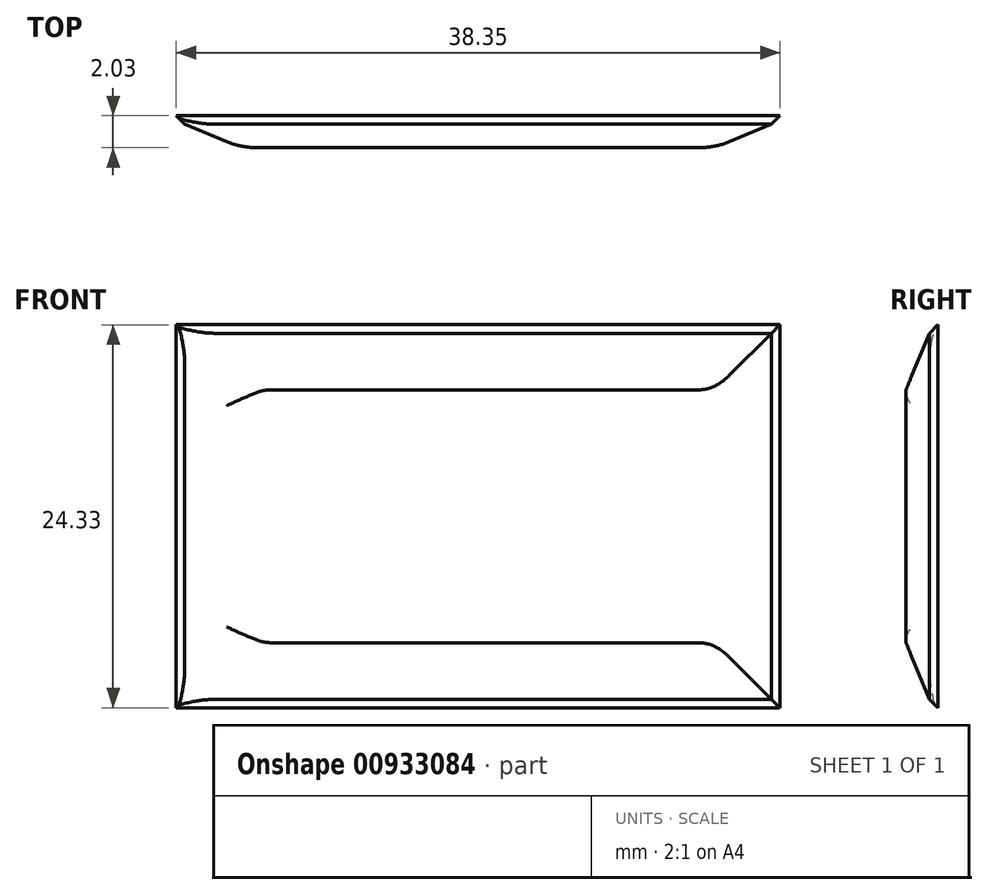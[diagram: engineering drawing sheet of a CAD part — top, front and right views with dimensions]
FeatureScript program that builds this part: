
annotation { "Feature Type Name" : "Feature", "Feature Type Description" : "" }
export const myFeature = defineFeature(function(context is Context, id is Id, definition is map)
    precondition{}
    {
        {
            var Q0;
            Q0=qCreatedBy(makeId("Front.planeOp"),FACE);
            var sketch = newSketch(context, id + "F0", { "sketchPlane" : qUnion([Q0])});
            skLineSegment(sketch, "E0.bottom", {"start": v(-54.75, 19.54) * mm, "end": v(-10.3, 19.54) * mm});
            skLineSegment(sketch, "E0.top", {"start": v(-54.75, -10.9) * mm, "end": v(-10.3, -10.9) * mm});
            skLineSegment(sketch, "E0.left", {"start": v(-54.75, 19.54) * mm, "end": v(-54.75, -10.9) * mm});
            skLineSegment(sketch, "E0.right", {"start": v(-10.3, 19.54) * mm, "end": v(-10.3, -10.9) * mm});
            skSolve(sketch);
        }
        {
            var Q0;
            Q0=makeQuery(id+"F0.imprint","IMPRINT",FACE,{"disambiguationData":[TD([[makeQuery(id+"F0.imprint","IMPRINT",EDGE,{"derivedFrom":sQuery(id+"F0.wireOp",EDGE,"E0.bottom")}),-1.0]])]});
            extrude(context, id + "F1", {"entities" : qUnion([Q0]), "depth" : 2.03 * mm, "offsetDistance" : 25.4 * mm});
        }
        {
            var Q0;
            Q0=makeQuery(id+"F1.opExtrude","CAP_FACE",FACE,{"disambiguationData":[OSD([sQuery(id+"F0.wireOp",EDGE,"E0.bottom"),sQuery(id+"F0.wireOp",EDGE,"E0.top"),sQuery(id+"F0.wireOp",EDGE,"E0.left"),sQuery(id+"F0.wireOp",EDGE,"E0.right")])],"isStart":false});
            chamfer(context, id + "F2", {"entities" : qUnion([Q0]), "width" : 5.08 * mm, "tangentPropagation" : true});
        }
        {
            var Q0;
            Q0=makeQuery(id+"F1.opExtrude","CAP_FACE",FACE,{"disambiguationData":[OSD([sQuery(id+"F0.wireOp",EDGE,"E0.bottom"),sQuery(id+"F0.wireOp",EDGE,"E0.top"),sQuery(id+"F0.wireOp",EDGE,"E0.left"),sQuery(id+"F0.wireOp",EDGE,"E0.right")])],"isStart":false});
            chamfer(context, id + "F3", {"entities" : qUnion([Q0]), "width" : 5.08 * mm, "tangentPropagation" : true});
        }
        {
            var Q0;
            {var subQ0=sQuery(id+"F0.wireOp",EDGE,"E0.left");var subQ1=sQuery(id+"F0.wireOp",EDGE,"E0.bottom");var subQ2=makeQuery(id+"F1.opExtrude","CAP_FACE",FACE,{"disambiguationData":[OSD([subQ1,sQuery(id+"F0.wireOp",EDGE,"E0.top"),subQ0,sQuery(id+"F0.wireOp",EDGE,"E0.right")])],"isStart":false});Q0=makeQuery(id+"F3.opChamfer","BLEND_EDGE",EDGE,{"blendedFrom":[makeQuery(id+"F2.opChamfer","BLEND_EDGE",EDGE,{"blendedFrom":[makeQuery(id+"F1.opExtrude","CAP_EDGE",EDGE,{"disambiguationData":[OSD([subQ1])],"isStart":false}),subQ2],"blendedInto":[subQ2]}),makeQuery(id+"F2.opChamfer","BLEND_EDGE",EDGE,{"blendedFrom":[makeQuery(id+"F1.opExtrude","CAP_EDGE",EDGE,{"disambiguationData":[OSD([subQ0])],"isStart":false}),subQ2],"blendedInto":[subQ2]})],"blendedInto":[]});}
            var Q1;
            {var subQ0=sQuery(id+"F0.wireOp",EDGE,"E0.left");var subQ1=sQuery(id+"F0.wireOp",EDGE,"E0.top");var subQ2=makeQuery(id+"F1.opExtrude","CAP_FACE",FACE,{"disambiguationData":[OSD([sQuery(id+"F0.wireOp",EDGE,"E0.bottom"),subQ1,subQ0,sQuery(id+"F0.wireOp",EDGE,"E0.right")])],"isStart":false});Q1=makeQuery(id+"F3.opChamfer","BLEND_EDGE",EDGE,{"blendedFrom":[makeQuery(id+"F2.opChamfer","BLEND_EDGE",EDGE,{"blendedFrom":[makeQuery(id+"F1.opExtrude","CAP_EDGE",EDGE,{"disambiguationData":[OSD([subQ1])],"isStart":false}),subQ2],"blendedInto":[subQ2]}),makeQuery(id+"F2.opChamfer","BLEND_EDGE",EDGE,{"blendedFrom":[makeQuery(id+"F1.opExtrude","CAP_EDGE",EDGE,{"disambiguationData":[OSD([subQ0])],"isStart":false}),subQ2],"blendedInto":[subQ2]})],"blendedInto":[]});}
            var Q2;
            {var subQ0=sQuery(id+"F0.wireOp",EDGE,"E0.right");var subQ1=sQuery(id+"F0.wireOp",EDGE,"E0.left");var subQ2=sQuery(id+"F0.wireOp",EDGE,"E0.top");var subQ3=sQuery(id+"F0.wireOp",EDGE,"E0.bottom");Q2=makeQuery(id+"F3.opChamfer","BLEND_EDGE",EDGE,{"blendedFrom":[makeQuery(id+"F2.opChamfer","BLEND_EDGE",EDGE,{"blendedFrom":[makeQuery(id+"F1.opExtrude","CAP_EDGE",EDGE,{"disambiguationData":[OSD([subQ1])],"isStart":false}),makeQuery(id+"F1.opExtrude","CAP_FACE",FACE,{"disambiguationData":[OSD([subQ3,subQ2,subQ1,subQ0])],"isStart":false})],"blendedInto":[makeQuery(id+"F1.opExtrude","CAP_FACE",FACE,{"disambiguationData":[OSD([subQ3,subQ2,subQ1,subQ0])],"isStart":false})]}),makeQuery(id+"F1.opExtrude","CAP_FACE",FACE,{"disambiguationData":[OSD([subQ3,subQ2,subQ1,subQ0])],"isStart":true})],"blendedInto":[makeQuery(id+"F1.opExtrude","CAP_FACE",FACE,{"disambiguationData":[OSD([subQ3,subQ2,subQ1,subQ0])],"isStart":true})]});}
            var Q3;
            {var subQ0=sQuery(id+"F0.wireOp",EDGE,"E0.left");var subQ1=makeQuery(id+"F1.opExtrude","CAP_FACE",FACE,{"disambiguationData":[OSD([sQuery(id+"F0.wireOp",EDGE,"E0.bottom"),sQuery(id+"F0.wireOp",EDGE,"E0.top"),subQ0,sQuery(id+"F0.wireOp",EDGE,"E0.right")])],"isStart":false});Q3=makeQuery(id+"F3.opChamfer","BLEND_EDGE",EDGE,{"blendedFrom":[makeQuery(id+"F2.opChamfer","BLEND_EDGE",EDGE,{"blendedFrom":[makeQuery(id+"F1.opExtrude","CAP_EDGE",EDGE,{"disambiguationData":[OSD([subQ0])],"isStart":false}),subQ1],"blendedInto":[subQ1]}),subQ1],"blendedInto":[subQ1]});}
            var Q4;
            {var subQ0=sQuery(id+"F0.wireOp",EDGE,"E0.right");var subQ1=makeQuery(id+"F1.opExtrude","CAP_FACE",FACE,{"disambiguationData":[OSD([sQuery(id+"F0.wireOp",EDGE,"E0.bottom"),sQuery(id+"F0.wireOp",EDGE,"E0.top"),sQuery(id+"F0.wireOp",EDGE,"E0.left"),subQ0])],"isStart":false});Q4=makeQuery(id+"F3.opChamfer","BLEND_EDGE",EDGE,{"blendedFrom":[makeQuery(id+"F2.opChamfer","BLEND_EDGE",EDGE,{"blendedFrom":[makeQuery(id+"F1.opExtrude","CAP_EDGE",EDGE,{"disambiguationData":[OSD([subQ0])],"isStart":false}),subQ1],"blendedInto":[subQ1]}),subQ1],"blendedInto":[subQ1]});}
            fillet(context, id + "F4", {"entities" : qUnion([Q0, Q1, Q2, Q3, Q4]), "radius" : 5.08 * mm, "tangentPropagation" : true, "allowEdgeOverflow" : false});
        }
    });
